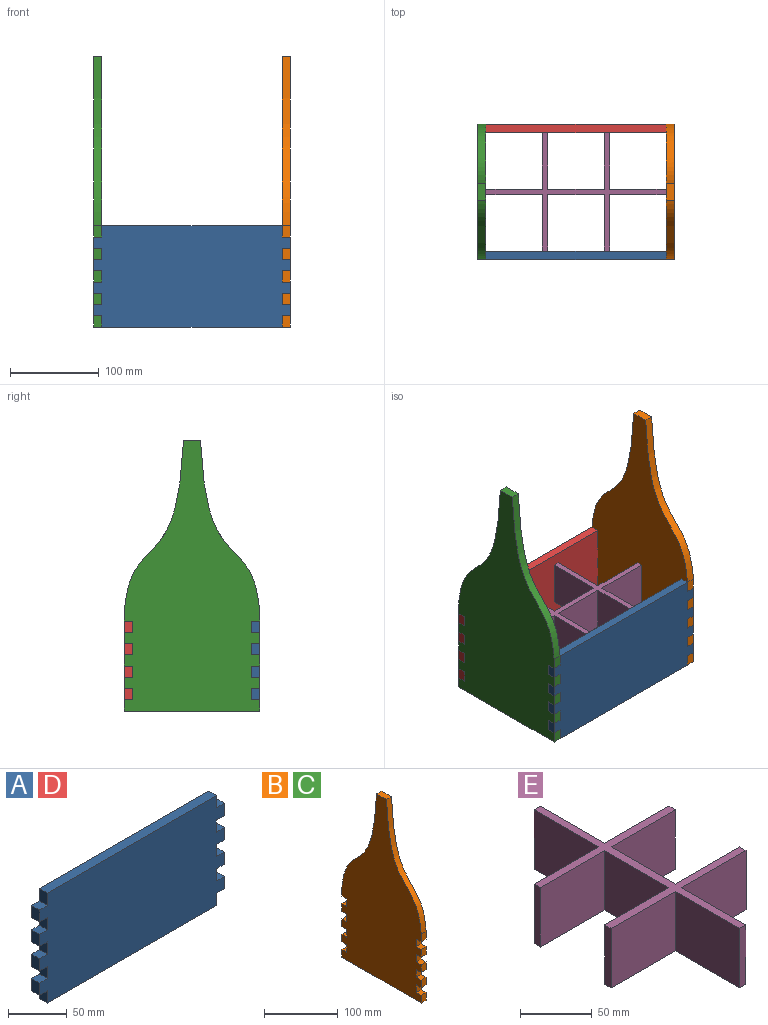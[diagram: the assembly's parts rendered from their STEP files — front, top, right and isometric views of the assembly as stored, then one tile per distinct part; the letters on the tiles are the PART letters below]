
ASSEMBLY  parts=5 mates=12
PART A: 38 faces, bbox 222.3x9.5x114.3 mm
  f0: plane 222.25x114.3mm, normal (0,-1,0), area 24193.5mm2, adj f1,f2,f3,f5,f6,f7,f8,f9
  f1: plane 203.2x9.53mm, normal (0,0,-1), area 1935.5mm2, adj f0,f4,f35,f36
  f2: plane 12.7x9.53mm, normal (1,0,0), area 121mm2, adj f0,f4,f28,f34
  f3: plane 12.7x9.53mm, normal (-1,0,0), area 121mm2, adj f0,f4,f31,f37
  f4: plane 222.25x114.3mm, normal (0,1,0), area 24193.5mm2, adj f1,f2,f3,f5,f6,f7,f8,f9
  f5: plane 12.7x9.53mm, normal (1,0,0), area 121mm2, adj f0,f4,f22,f29
  f6: plane 12.7x9.53mm, normal (-1,0,0), area 121mm2, adj f0,f4,f25,f33
  f7: plane 12.7x9.53mm, normal (1,0,0), area 121mm2, adj f0,f4,f16,f23
  f8: plane 12.7x9.53mm, normal (-1,0,0), area 121mm2, adj f0,f4,f19,f27
  f9: plane 12.7x9.53mm, normal (1,0,0), area 121mm2, adj f0,f4,f12,f17
  f10: plane 12.7x9.53mm, normal (-1,0,0), area 121mm2, adj f0,f4,f14,f21
  f11: plane 203.2x9.53mm, normal (0,0,1), area 1935.5mm2, adj f0,f4,f13,f15
  f12: plane 9.53x9.53mm, normal (0,0,1), area 90.7mm2, adj f0,f4,f9,f13
  f13: plane 12.7x9.53mm, normal (1,0,0), area 121mm2, adj f0,f4,f11,f12
  f14: plane 9.53x9.53mm, normal (0,0,1), area 90.7mm2, adj f0,f4,f10,f15
  f15: plane 12.7x9.53mm, normal (-1,0,0), area 121mm2, adj f0,f4,f11,f14
  f16: plane 9.53x9.53mm, normal (0,0,1), area 90.7mm2, adj f0,f4,f7,f18
  f17: plane 9.53x9.53mm, normal (0,0,-1), area 90.7mm2, adj f0,f4,f9,f18
  f18: plane 12.7x9.53mm, normal (1,0,0), area 121mm2, adj f0,f4,f16,f17
  f19: plane 9.53x9.53mm, normal (0,0,1), area 90.7mm2, adj f0,f4,f8,f20
  f20: plane 12.7x9.53mm, normal (-1,0,0), area 121mm2, adj f0,f4,f19,f21
  f21: plane 9.53x9.53mm, normal (0,0,-1), area 90.7mm2, adj f0,f4,f10,f20
  f22: plane 9.53x9.53mm, normal (0,0,1), area 90.7mm2, adj f0,f4,f5,f24
  f23: plane 9.53x9.53mm, normal (0,0,-1), area 90.7mm2, adj f0,f4,f7,f24
  f24: plane 12.7x9.53mm, normal (1,0,0), area 121mm2, adj f0,f4,f22,f23
  f25: plane 9.53x9.53mm, normal (0,0,1), area 90.7mm2, adj f0,f4,f6,f26
  f26: plane 12.7x9.53mm, normal (-1,0,0), area 121mm2, adj f0,f4,f25,f27
  f27: plane 9.53x9.53mm, normal (0,0,-1), area 90.7mm2, adj f0,f4,f8,f26
  f28: plane 9.53x9.53mm, normal (0,0,1), area 90.7mm2, adj f0,f2,f4,f30
  f29: plane 9.53x9.53mm, normal (0,0,-1), area 90.7mm2, adj f0,f4,f5,f30
  f30: plane 12.7x9.53mm, normal (1,0,0), area 121mm2, adj f0,f4,f28,f29
  f31: plane 9.53x9.53mm, normal (0,0,1), area 90.7mm2, adj f0,f3,f4,f32
  f32: plane 12.7x9.53mm, normal (-1,0,0), area 121mm2, adj f0,f4,f31,f33
  f33: plane 9.53x9.53mm, normal (0,0,-1), area 90.7mm2, adj f0,f4,f6,f32
  f34: plane 9.53x9.53mm, normal (0,0,-1), area 90.7mm2, adj f0,f2,f4,f35
  f35: plane 12.7x9.53mm, normal (1,0,0), area 121mm2, adj f0,f1,f4,f34
  f36: plane 12.7x9.53mm, normal (-1,0,0), area 121mm2, adj f0,f1,f4,f37
  f37: plane 9.53x9.53mm, normal (0,0,-1), area 90.7mm2, adj f0,f3,f4,f36
PART B: 40 faces, bbox 9.5x152.4x304.8 mm
  f0: plane 12.7x9.53mm, normal (0,1,0), area 121mm2, adj f2,f11,f26,f27
  f1: plane 12.7x9.53mm, normal (0,-1,0), area 121mm2, adj f7,f13,f26,f27
  f2: plane 9.53x9.53mm, normal (0,0,-1), area 90.7mm2, adj f0,f4,f26,f27
  f3: plane 9.53x9.53mm, normal (0,0,1), area 90.7mm2, adj f4,f24,f26,f27
  f4: plane 12.7x9.53mm, normal (0,1,0), area 121mm2, adj f2,f3,f26,f27
  f5: plane 9.53x9.53mm, normal (0,0,1), area 90.7mm2, adj f6,f25,f26,f27
  f6: plane 12.7x9.53mm, normal (0,-1,0), area 121mm2, adj f5,f7,f26,f27
  f7: plane 9.53x9.53mm, normal (0,0,-1), area 90.7mm2, adj f1,f6,f26,f27
  f8: plane 12.7x9.53mm, normal (0,1,0), area 121mm2, adj f10,f19,f26,f27
  f9: plane 12.7x9.53mm, normal (0,-1,0), area 121mm2, adj f15,f21,f26,f27
  f10: plane 9.53x9.53mm, normal (0,0,-1), area 90.7mm2, adj f8,f12,f26,f27
  f11: plane 9.53x9.53mm, normal (0,0,1), area 90.7mm2, adj f0,f12,f26,f27
  f12: plane 12.7x9.53mm, normal (0,1,0), area 121mm2, adj f10,f11,f26,f27
  f13: plane 9.53x9.53mm, normal (0,0,1), area 90.7mm2, adj f1,f14,f26,f27
  f14: plane 12.7x9.53mm, normal (0,-1,0), area 121mm2, adj f13,f15,f26,f27
  f15: plane 9.53x9.53mm, normal (0,0,-1), area 90.7mm2, adj f9,f14,f26,f27
  f16: plane 12.7x9.53mm, normal (0,1,0), area 121mm2, adj f18,f26,f27,f35
  f17: plane 12.7x9.53mm, normal (0,-1,0), area 121mm2, adj f23,f26,f27,f39
  f18: plane 9.53x9.53mm, normal (0,0,-1), area 90.7mm2, adj f16,f20,f26,f27
  f19: plane 9.53x9.53mm, normal (0,0,1), area 90.7mm2, adj f8,f20,f26,f27
  f20: plane 12.7x9.53mm, normal (0,1,0), area 121mm2, adj f18,f19,f26,f27
  f21: plane 9.53x9.53mm, normal (0,0,1), area 90.7mm2, adj f9,f22,f26,f27
  f22: plane 12.7x9.53mm, normal (0,-1,0), area 121mm2, adj f21,f23,f26,f27
  f23: plane 9.53x9.53mm, normal (0,0,-1), area 90.7mm2, adj f17,f22,f26,f27
  f24: plane 12.7x9.53mm, normal (0,1,0), area 121mm2, adj f3,f26,f27,f29
  f25: plane 12.7x9.53mm, normal (0,-1,0), area 121mm2, adj f5,f26,f27,f29
  f26: plane 304.8x152.4mm, normal (1,0,0), area 30161.6mm2, adj f0,f1,f2,f3,f4,f5,f6,f7
  f27: plane 304.8x152.4mm, normal (-1,0,0), area 30161.6mm2, adj f0,f1,f2,f3,f4,f5,f6,f7
  f28: plane 19.05x9.53mm, normal (0,0,1), area 181.5mm2, adj f26,f27,f32,f33
  f29: plane 152.4x9.53mm, normal (0,0,-1), area 1451.6mm2, adj f24,f25,f26,f27
  f30: plane 12.7x9.53mm, normal (0,1,0), area 121mm2, adj f26,f27,f32,f34
  f31: plane 12.7x9.53mm, normal (0,-1,0), area 121mm2, adj f26,f27,f33,f37
  f32: extruded ~190.5x66.68mm, area 1977.4mm2, adj f26,f27,f28,f30
  f33: extruded ~190.5x66.68mm, area 1977.4mm2, adj f26,f27,f28,f31
  f34: plane 9.53x9.53mm, normal (0,0,-1), area 90.7mm2, adj f26,f27,f30,f36
  f35: plane 9.53x9.53mm, normal (0,0,1), area 90.7mm2, adj f16,f26,f27,f36
  f36: plane 12.7x9.53mm, normal (0,1,0), area 121mm2, adj f26,f27,f34,f35
  f37: plane 9.53x9.53mm, normal (0,0,-1), area 90.7mm2, adj f26,f27,f31,f38
  f38: plane 12.7x9.53mm, normal (0,-1,0), area 121mm2, adj f26,f27,f37,f39
  f39: plane 9.53x9.53mm, normal (0,0,1), area 90.7mm2, adj f17,f26,f27,f38
PART C: same geometry as B
PART D: same geometry as A
PART E: 22 faces, bbox 133.4x203.2x50.8 mm
  f0: plane 50.8x6.35mm, normal (0,1,0), area 322.6mm2, adj f1,f19,f20,f21
  f1: plane 63.5x50.8mm, normal (-1,0,0), area 3225.8mm2, adj f0,f2,f20,f21
  f2: plane 63.5x50.8mm, normal (0,1,0), area 3225.8mm2, adj f1,f3,f20,f21
  f3: plane 50.8x6.35mm, normal (-1,0,0), area 322.6mm2, adj f2,f4,f20,f21
  f4: plane 63.5x50.8mm, normal (0,-1,0), area 3225.8mm2, adj f3,f5,f20,f21
  f5: plane 63.5x50.8mm, normal (-1,0,0), area 3225.8mm2, adj f4,f6,f20,f21
  f6: plane 63.5x50.8mm, normal (0,1,0), area 3225.8mm2, adj f5,f7,f20,f21
  f7: plane 50.8x6.35mm, normal (-1,0,0), area 322.6mm2, adj f6,f8,f20,f21
  f8: plane 63.5x50.8mm, normal (0,-1,0), area 3225.8mm2, adj f7,f9,f20,f21
  f9: plane 63.5x50.8mm, normal (-1,0,0), area 3225.8mm2, adj f8,f10,f20,f21
  f10: plane 50.8x6.35mm, normal (0,-1,0), area 322.6mm2, adj f9,f11,f20,f21
  f11: plane 63.5x50.8mm, normal (1,0,0), area 3225.8mm2, adj f10,f12,f20,f21
  f12: plane 63.5x50.8mm, normal (0,-1,0), area 3225.8mm2, adj f11,f13,f20,f21
  f13: plane 50.8x6.35mm, normal (1,0,0), area 322.6mm2, adj f12,f14,f20,f21
  f14: plane 63.5x50.8mm, normal (0,1,0), area 3225.8mm2, adj f13,f15,f20,f21
  f15: plane 63.5x50.8mm, normal (1,0,0), area 3225.8mm2, adj f14,f16,f20,f21
  f16: plane 63.5x50.8mm, normal (0,-1,0), area 3225.8mm2, adj f15,f17,f20,f21
  f17: plane 50.8x6.35mm, normal (1,0,0), area 322.6mm2, adj f16,f18,f20,f21
  f18: plane 63.5x50.8mm, normal (0,1,0), area 3225.8mm2, adj f17,f19,f20,f21
  f19: plane 63.5x50.8mm, normal (1,0,0), area 3225.8mm2, adj f0,f18,f20,f21
  f20: plane 203.2x133.35mm, normal (0,0,1), area 2903.2mm2, adj f0,f1,f2,f3,f4,f5,f6,f7
  f21: plane 203.2x133.35mm, normal (0,0,-1), area 2903.2mm2, adj f0,f1,f2,f3,f4,f5,f6,f7
PLACE A t=(134.57,21.62,108.72)mm
PLACE B t=(125.05,164.5,108.72)mm
PLACE C t=(-87.68,164.5,108.72)mm
PLACE D t=(134.57,164.5,108.72)mm
PLACE E rot(axis=(0,0,-1),90deg) t=(23.45,88.3,159.52)mm
MATE planar E.f20 <-> D.f14  axis (0,0,1) through (55.2,85.12,210.32)mm
MATE planar A.f1 <-> C.f29  axis (0,0,-1) through (23.45,16.86,108.72)mm
MATE planar B.f29 <-> A.f1  axis (0,0,-1) through (129.81,88.3,108.72)mm
MATE planar A.f0 <-> C.f31  axis (0,-1,0) through (23.45,12.1,165.87)mm
MATE planar C.f27 <-> A.f10  axis (-1,0,0) through (-87.68,88.3,218.93)mm
MATE planar D.f10 <-> C.f27  axis (-1,0,0) through (-87.68,159.73,203.97)mm
MATE planar C.f29 <-> D.f1  axis (0,0,-1) through (-82.92,88.3,108.72)mm
MATE planar E.f13 <-> A.f4  axis (0,-1,0) through (-11.48,21.62,184.92)mm
MATE planar B.f31 <-> A.f0  axis (0,-1,0) through (129.81,12.1,216.67)mm
MATE planar B.f26 <-> A.f9  axis (1,0,0) through (134.57,88.3,108.72)mm
MATE planar E.f10 <-> C.f26  axis (-1,0,0) through (-78.15,88.3,184.92)mm
MATE planar C.f30 <-> D.f4  axis (0,1,0) through (-82.92,164.5,216.67)mm
